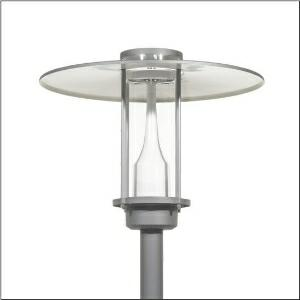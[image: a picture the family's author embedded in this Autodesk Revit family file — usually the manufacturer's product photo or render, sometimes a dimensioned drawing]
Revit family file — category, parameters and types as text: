
# Revit family: city-light_plus_iq___p1_0a_5xa5275bf14hp_a9e6
name_source: partatom
category: Lighting Fixtures
units: mm (PartAtom-declared; Revit-internal decimal feet)

## family parameters
Cut with Voids When Loaded = No
Host = Face
Light Source = No
Part Type = Normal
Room Calculation Point = No
Round Connector Dimension = Use Diameter
Shared = No

## types (1)
- --- (1 x LED, 3710 lm, 33.6 W, 2200K)
    Apparent Load = 34 VA
    CIE Flux Codes = 30 60 90 96 100
    Color Rendering = 70
    Color Temperature = 2200K
    Default Elevation = 1800 mm
    Description = City-Light Plus iQ, mast luminaire, Module 540 iQ-SR, primary light control with 3 zone facetted reflector, of plastic, silver coated, highly specular, structured, primary optical cover: cover, of PMMA, transparent, light distribution: P1.0a, light emission: direct distribution, primary light characteristic: strongly asymmetric, installation type: post-top, LED, High Power LED, rated luminous flux: 3.710lm, luminous efficacy: 110lm/W, light colour: 722, colour temperature: 2200K, control gear: iQ Street-Remote, control: pre-setting: logarithmic dimming characteristic, Street-Remote, Auto-Match, Temp-Guard, Lumen-Switch, Night-Set, Smart-Wire, Light-Fading, Desk-Remote (wireless, voltage-free reading and setting of iQ features in the workshop via application-optimized NFC function/RFID function), optimised constant luminous flux control (CLO 2.0), with terminal, 6-pole, max. 2.5mm², mains connection: 230..240V, AC, 50/60Hz, start of lifetime: 34W, end of service life: 36W, reduction: 15W, luminaire housing, upper part, of glass-fibre reinforced polyester, coated, Siteco® metallic grey (DB 702S), diameter: 750mm, height: 590mm, spigot size: d x l = 76 x 70mm (post-top) | with reducer (optional accessory) 60 x 70mm, mounting height: 3..5m, post-top mast mounting element, of diecast aluminium, coated, Siteco® metallic grey (DB 702S), Module 540 iQ-SR, traffic white (RAL 9016), equipment: Power, protection rating (complete): IP65, insulation class (complete): insulation class II (safety insulation), certification: CE, ENEC, VDE, packaging unit: 1 piece

Light Distribution: P1.0a
    Height = 590 mm
    Lamp = 1 x LED
    Lamp Light Flux = 3710 lm
    Lamp Power = 33.6 W
    Lamp count = 1
    Length = 750 mm
    Luminous efficacy = 110 lm/W
    Manufacturer = Siteco
    ModVariant = No
    Model = 5XA5275BF14HP
    Number of Poles = 1
    OnlyDefault = Yes
    Power Factor = 1
    Product Name = City-Light Plus iQ | P1.0a
    Product group = mast luminaire | pylon top
    ProductGroupID = 6100
    Protection Class = Protection class II
    Protection Degree = IP 65
    RLX_Detail_Level = 1
    RLX_Emergency_Light_Flux = 0 lm
    RLX_Emergency_Type = 0
    RLX_Emergency_Type_DB = No
    RlxData = <blob elided: 35057 chars, md5=3276c07b>
    Socket = socket
    Standby Power = 0 W
    System Light Flux = 3710 lm
    System Power = 34 W
    Type Comments = factory setting: luminous flux: 100 % | dim-lin: 254 | 695 mA
    Type Image = l_1006456.jpg
    URL = http://relux.com
    VarID = @adj_215073
    Voltage = 0 V
    Weight = 0.00 kg
    Width = 0 mm  [stored 0 ft]

note: [stored X ft] marks values corroborated as IEEE doubles in the binary element streams (Revit-internal decimal feet)

## geometry (parser evidence)
native form markers: Blend x4, Sweep x10
no freeform markers — native parametric forms only
